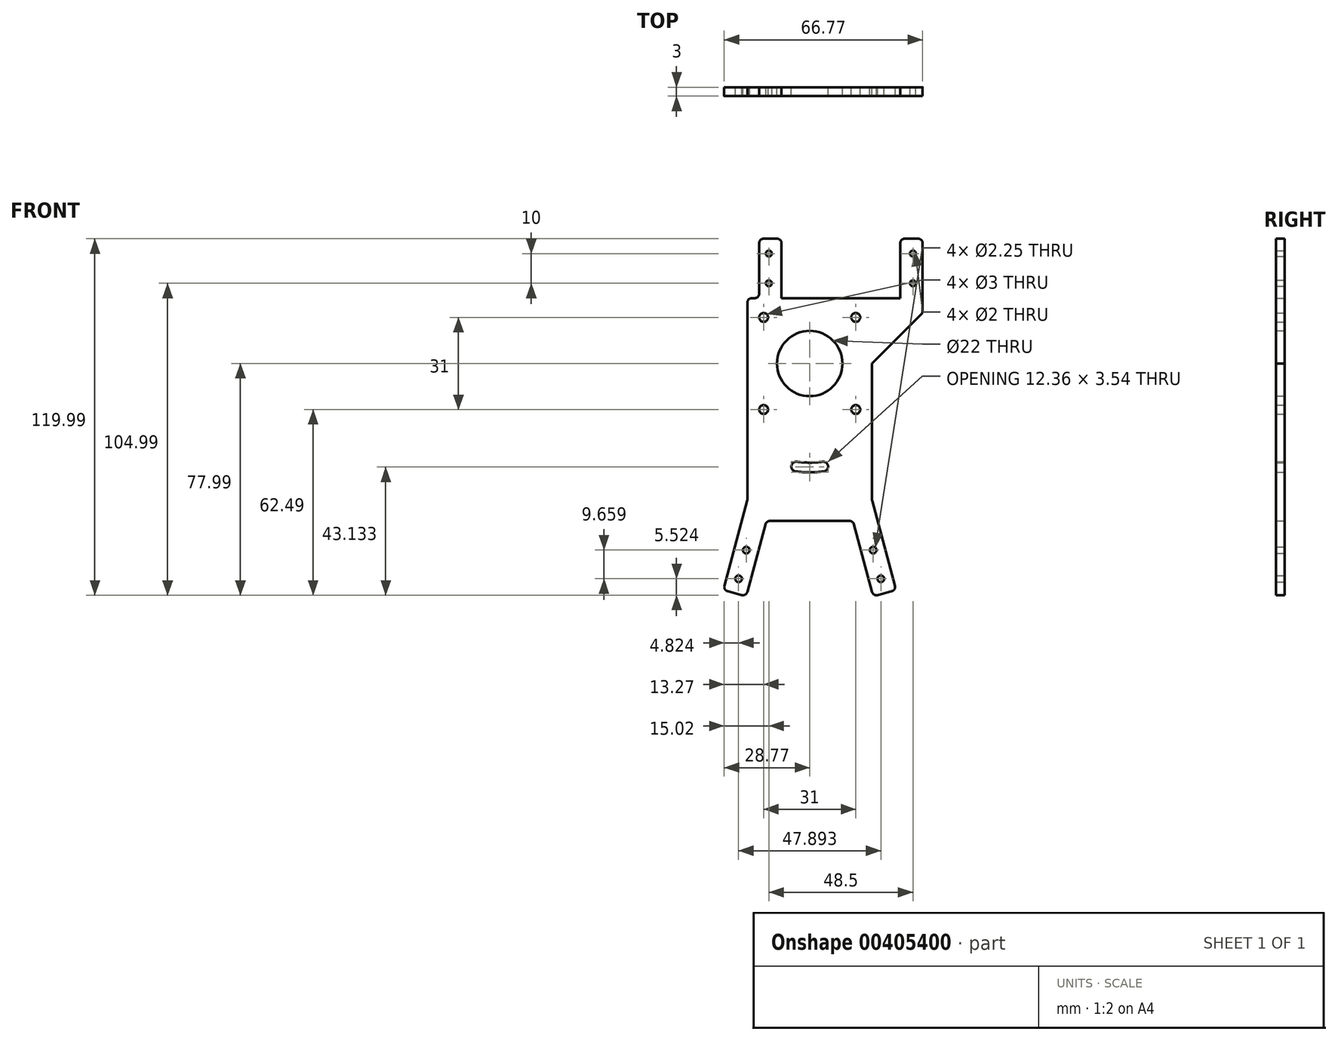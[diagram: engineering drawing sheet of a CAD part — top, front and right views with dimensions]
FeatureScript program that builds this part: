
annotation { "Feature Type Name" : "Feature", "Feature Type Description" : "" }
export const myFeature = defineFeature(function(context is Context, id is Id, definition is map)
    precondition{}
    {
        {
            var Q0;
            Q0=qCreatedBy(makeId("Front.planeOp"),FACE);
            var sketch = newSketch(context, id + "F0", { "sketchPlane" : qUnion([Q0])});
            skLineSegment(sketch, "E0", {"start": v(0, 41.33) * mm, "end": v(0, -11.3) * mm, "construction": true});
            skLineSegment(sketch, "E1", {"start": v(16.28, 32) * mm, "end": v(-17.99, 32) * mm, "construction": true});
            skCircle(sketch, "E2", {"center": v(-4.25, 32) * mm, "radius": 11.5 * mm, "construction": true});
            skCircle(sketch, "E3", {"center": v(0, 36.25) * mm, "radius": 11.5 * mm, "construction": true});
            skCircle(sketch, "E4", {"center": v(4.25, 32) * mm, "radius": 11.5 * mm, "construction": true});
            skSolve(sketch);
        }
        {
            var Q0;
            Q0=qCreatedBy(makeId("Front.planeOp"),FACE);
            var sketch = newSketch(context, id + "F1", { "sketchPlane" : qUnion([Q0])});
            skArc(sketch, "E5", {"start": v(0, 11) * mm, "mid": v(11, 0) * mm, "end": v(0, -11) * mm});
            skCircle(sketch, "E6", {"center": v(15.5, 15.5) * mm, "radius": 1.5 * mm});
            skCircle(sketch, "E7", {"center": v(15.5, -15.5) * mm, "radius": 1.5 * mm});
            skLineSegment(sketch, "E8", {"start": v(0, 22) * mm, "end": v(21, 22) * mm});
            skLineSegment(sketch, "E9", {"start": v(29.1, -76.26) * mm, "end": v(21.38, -78.33) * mm});
            skLineSegment(sketch, "E10", {"start": v(14.59, -53) * mm, "end": v(0, -53) * mm});
            skLineSegment(sketch, "E11", {"start": v(14.59, -53) * mm, "end": v(21.38, -78.33) * mm});
            skLineSegment(sketch, "E12", {"start": v(21, -46.01) * mm, "end": v(29.1, -76.26) * mm});
            skLineSegment(sketch, "E13", {"start": v(21, -46.01) * mm, "end": v(21, 22) * mm});
            skLineSegment(sketch, "E14", {"start": v(-10.7, 0) * mm, "end": v(32.43, 0) * mm, "construction": true});
            skCircle(sketch, "E15", {"center": v(0, 0) * mm, "radius": 3.5 * mm, "construction": true});
            skPoint(sketch, "E16", {"position": v(0, -53) * mm});
            skArc(sketch, "E17", {"start": v(4.36, -33.09) * mm, "mid": v(2.18, -33.3) * mm, "end": v(0, -33.38) * mm});
            skArc(sketch, "E18", {"start": v(4.78, -36.31) * mm, "mid": v(2.4, -36.55) * mm, "end": v(0, -36.62) * mm});
            skLineSegment(sketch, "E19", {"start": v(0, 0) * mm, "end": v(4.78, -36.31) * mm, "construction": true});
            skArc(sketch, "E20", {"start": v(4.36, -33.09) * mm, "mid": v(6.18, -34.49) * mm, "end": v(4.78, -36.31) * mm});
            skLineSegment(sketch, "E21", {"start": v(-2.2, 25.14) * mm, "end": v(26.06, -80.37) * mm, "construction": true});
            skLineSegment(sketch, "E22", {"start": v(1.7, 7.16) * mm, "end": v(7.74, -15.37) * mm, "construction": true});
            skLineSegment(sketch, "E23", {"start": v(3.52, 7.16) * mm, "end": v(9.55, -15.37) * mm, "construction": true});
            skLineSegment(sketch, "E24", {"start": v(0, 22) * mm, "end": v(0, 11) * mm});
            skLineSegment(sketch, "E25", {"start": v(0, -11) * mm, "end": v(0, -33.38) * mm});
            skLineSegment(sketch, "E26", {"start": v(0, -36.62) * mm, "end": v(0, -53) * mm});
            skArc(sketch, "E27", {"start": v(8.15, -34.04) * mm, "mid": v(3.11, -34.86) * mm, "end": v(-2, -34.94) * mm, "construction": true});
            skCircle(sketch, "E28", {"center": v(23.95, -72.47) * mm, "radius": 1.13 * mm});
            skCircle(sketch, "E29", {"center": v(21.36, -62.8) * mm, "radius": 1.13 * mm});
            skCircle(sketch, "E30", {"center": v(27.5, -31.5) * mm, "radius": 1.16 * mm, "construction": true});
            skSolve(sketch);
        }
        {
            var Q0;
            Q0=qSketchRegion(id+"F1",true);
            extrude(context, id + "F2", {"entities" : qUnion([Q0]), "depth" : 3 * mm});
        }
        {
            var Q0;
            Q0=makeQuery(id+"F2.opExtrude","SWEPT_BODY",BODY,{"disambiguationData":[OSD([sQuery(id+"F1.wireOp",EDGE,"E5"),sQuery(id+"F1.wireOp",EDGE,"E6"),sQuery(id+"F1.wireOp",EDGE,"E7"),sQuery(id+"F1.wireOp",EDGE,"E8"),sQuery(id+"F1.wireOp",EDGE,"E9"),sQuery(id+"F1.wireOp",EDGE,"E10"),sQuery(id+"F1.wireOp",EDGE,"E11"),sQuery(id+"F1.wireOp",EDGE,"E12"),sQuery(id+"F1.wireOp",EDGE,"E13"),sQuery(id+"F1.wireOp",EDGE,"794e9613-435e-44ef-8f0d-1ea17954f1a4"),sQuery(id+"F1.wireOp",EDGE,"7908c58d-3949-49cd-819e-191e6de99807"),sQuery(id+"F1.wireOp",EDGE,"71a8888d-9325-4b5b-85cc-ae257d3d2673"),sQuery(id+"F1.wireOp",EDGE,"8b422214-139a-407f-9bb9-311ab375745e"),sQuery(id+"F1.wireOp",EDGE,"e21d943d-84f5-4bef-b377-ec38a9bf888f"),sQuery(id+"F1.wireOp",EDGE,"7b2084c7-02a4-4d11-939f-4f07836c72c3"),sQuery(id+"F1.wireOp",EDGE,"E17"),sQuery(id+"F1.wireOp",EDGE,"E18"),sQuery(id+"F1.wireOp",EDGE,"E20"),sQuery(id+"F1.wireOp",EDGE,"E24"),sQuery(id+"F1.wireOp",EDGE,"E25"),sQuery(id+"F1.wireOp",EDGE,"E26")])]});
            var Q1;
            Q1=makeQuery(id+"F2.opExtrude","SWEPT_FACE",FACE,{"disambiguationData":[OSD([sQuery(id+"F1.wireOp",EDGE,"E25")])]});
            mirror(context, id + "F3", {"operationType" : NewBodyOperationType.ADD, "entities" : qUnion([Q0]), "mirrorPlane" : qUnion([Q1])});
        }
        {
            var Q0;
            Q0=qCreatedBy(makeId("Front.planeOp"),FACE);
            var sketch = newSketch(context, id + "F4", { "sketchPlane" : qUnion([Q0])});
            skLineSegment(sketch, "E31", {"start": v(38, 42) * mm, "end": v(38, 17) * mm});
            skLineSegment(sketch, "E32", {"start": v(38, 17) * mm, "end": v(21, 0) * mm});
            skLineSegment(sketch, "E33", {"start": v(38, 42) * mm, "end": v(30.5, 42) * mm});
            skLineSegment(sketch, "E34", {"start": v(30.5, 22) * mm, "end": v(30.5, 42) * mm});
            skCircle(sketch, "E35", {"center": v(34.75, 27) * mm, "radius": 1 * mm});
            skCircle(sketch, "E36", {"center": v(34.75, 37) * mm, "radius": 1 * mm});
            skLineSegment(sketch, "E37", {"start": v(30.5, 22) * mm, "end": v(21, 22) * mm});
            skLineSegment(sketch, "E38", {"start": v(21, 22) * mm, "end": v(21, 0) * mm});
            skLineSegment(sketch, "E39", {"start": v(-17, 42) * mm, "end": v(-17, 22) * mm});
            skCircle(sketch, "E40.MirrorC", {"center": v(-13.75, 27) * mm, "radius": 1 * mm});
            skCircle(sketch, "E41.MirrorC", {"center": v(-13.75, 37) * mm, "radius": 1 * mm});
            skLineSegment(sketch, "E42.MirrorCS", {"start": v(-9.5, 22) * mm, "end": v(-9.5, 42) * mm});
            skLineSegment(sketch, "E43.MirrorCS", {"start": v(-17, 42) * mm, "end": v(-9.5, 42) * mm});
            skLineSegment(sketch, "E44", {"start": v(-17, 22) * mm, "end": v(-9.5, 22) * mm});
            skSolve(sketch);
        }
        {
            var Q0;
            Q0=qSketchRegion(id+"F4",true);
            extrude(context, id + "F5", {"entities" : qUnion([Q0]), "operationType" : NewBodyOperationType.ADD, "depth" : 3 * mm});
        }
        {
            var Q0;
            Q0=makeQuery(id+"F3.opPattern","COPY",EDGE,{"derivedFrom":makeQuery(id+"F2.opExtrude","SWEPT_EDGE",EDGE,{"disambiguationData":[OSD([sQuery(id+"F1.wireOp",EDGE,"E8"),sQuery(id+"F1.wireOp",EDGE,"E13")])]}),"instanceName":"1"});
            var Q1;
            Q1=makeQuery(id+"F5.opExtrude","SWEPT_EDGE",EDGE,{"disambiguationData":[OSD([sQuery(id+"F4.wireOp",EDGE,"E39"),sQuery(id+"F4.wireOp",EDGE,"E43.MirrorCS")])]});
            var Q2;
            Q2=makeQuery(id+"F5.opExtrude","SWEPT_EDGE",EDGE,{"disambiguationData":[OSD([sQuery(id+"F4.wireOp",EDGE,"E42.MirrorCS"),sQuery(id+"F4.wireOp",EDGE,"E43.MirrorCS")])]});
            var Q3;
            Q3=makeQuery(id+"F5.opExtrude","SWEPT_EDGE",EDGE,{"disambiguationData":[OSD([sQuery(id+"F4.wireOp",EDGE,"E33"),sQuery(id+"F4.wireOp",EDGE,"E34")])]});
            var Q4;
            Q4=makeQuery(id+"F5.opExtrude","SWEPT_EDGE",EDGE,{"disambiguationData":[OSD([sQuery(id+"F4.wireOp",EDGE,"E31"),sQuery(id+"F4.wireOp",EDGE,"E33")])]});
            var Q5;
            Q5=makeQuery(id+"F5.opExtrude","SWEPT_EDGE",EDGE,{"disambiguationData":[OSD([sQuery(id+"F4.wireOp",EDGE,"E31"),sQuery(id+"F4.wireOp",EDGE,"E32")])]});
            var Q6;
            Q6=makeQuery(id+"F5.opExtrude","SWEPT_EDGE",EDGE,{"disambiguationData":[OSD([sQuery(id+"F4.wireOp",EDGE,"E32"),sQuery(id+"F4.wireOp",EDGE,"E38")])]});
            var Q7;
            Q7=makeQuery(id+"F2.opExtrude","SWEPT_EDGE",EDGE,{"disambiguationData":[OSD([sQuery(id+"F1.wireOp",EDGE,"E12"),sQuery(id+"F1.wireOp",EDGE,"E13")])]});
            var Q8;
            Q8=makeQuery(id+"F2.opExtrude","SWEPT_EDGE",EDGE,{"disambiguationData":[OSD([sQuery(id+"F1.wireOp",EDGE,"E9"),sQuery(id+"F1.wireOp",EDGE,"E12")])]});
            var Q9;
            Q9=makeQuery(id+"F2.opExtrude","SWEPT_EDGE",EDGE,{"disambiguationData":[OSD([sQuery(id+"F1.wireOp",EDGE,"E9"),sQuery(id+"F1.wireOp",EDGE,"E11")])]});
            var Q10;
            Q10=makeQuery(id+"F3.opPattern","COPY",EDGE,{"derivedFrom":makeQuery(id+"F2.opExtrude","SWEPT_EDGE",EDGE,{"disambiguationData":[OSD([sQuery(id+"F1.wireOp",EDGE,"E10"),sQuery(id+"F1.wireOp",EDGE,"E11")])]}),"instanceName":"1"});
            var Q11;
            Q11=makeQuery(id+"F3.opPattern","COPY",EDGE,{"derivedFrom":makeQuery(id+"F2.opExtrude","SWEPT_EDGE",EDGE,{"disambiguationData":[OSD([sQuery(id+"F1.wireOp",EDGE,"E9"),sQuery(id+"F1.wireOp",EDGE,"E11")])]}),"instanceName":"1"});
            var Q12;
            Q12=makeQuery(id+"F3.opPattern","COPY",EDGE,{"derivedFrom":makeQuery(id+"F2.opExtrude","SWEPT_EDGE",EDGE,{"disambiguationData":[OSD([sQuery(id+"F1.wireOp",EDGE,"E9"),sQuery(id+"F1.wireOp",EDGE,"E12")])]}),"instanceName":"1"});
            var Q13;
            Q13=makeQuery(id+"F2.opExtrude","SWEPT_EDGE",EDGE,{"disambiguationData":[OSD([sQuery(id+"F1.wireOp",EDGE,"E10"),sQuery(id+"F1.wireOp",EDGE,"E11")])]});
            var Q14;
            Q14=makeQuery(id+"F3.opPattern","COPY",EDGE,{"derivedFrom":makeQuery(id+"F2.opExtrude","SWEPT_EDGE",EDGE,{"disambiguationData":[OSD([sQuery(id+"F1.wireOp",EDGE,"E12"),sQuery(id+"F1.wireOp",EDGE,"E13")])]}),"instanceName":"1"});
            var Q15;
            Q15=makeQuery(id+"F5.opExtrude","SWEPT_EDGE",EDGE,{"disambiguationData":[OSD([sQuery(id+"F4.wireOp",EDGE,"E39"),sQuery(id+"F4.wireOp",EDGE,"E44")])]});
            fillet(context, id + "F6", {"entities" : qUnion([Q0, Q1, Q2, Q3, Q4, Q5, Q6, Q7, Q8, Q9, Q10, Q11, Q12, Q13, Q14, Q15]), "radius" : 1.5 * mm, "tangentPropagation" : true, "allowEdgeOverflow" : false});
        }
    });
